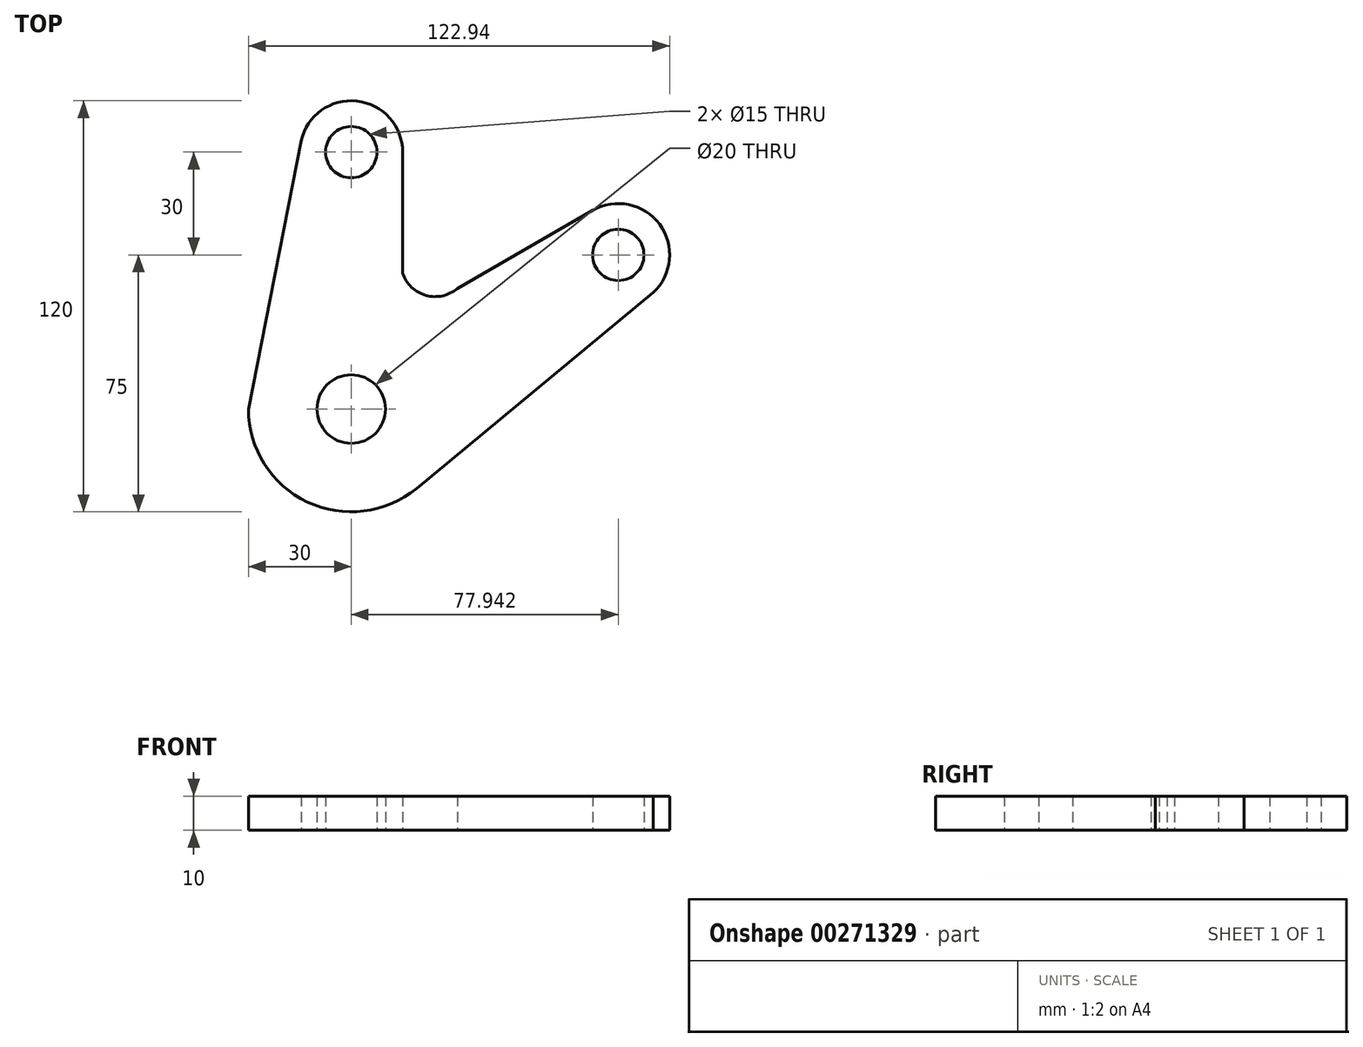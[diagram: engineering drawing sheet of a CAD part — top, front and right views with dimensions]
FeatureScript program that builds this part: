
annotation { "Feature Type Name" : "Feature", "Feature Type Description" : "" }
export const myFeature = defineFeature(function(context is Context, id is Id, definition is map)
    precondition{}
    {
        {
            var Q0;
            Q0=qCreatedBy(makeId("Top.planeOp"),FACE);
            var sketch = newSketch(context, id + "F0", { "sketchPlane" : qUnion([Q0])});
            skCircle(sketch, "E0", {"center": v(0, 0) * mm, "radius": 10 * mm});
            skLineSegment(sketch, "E1", {"start": v(0, 0) * mm, "end": v(77.94, 45) * mm, "construction": true});
            skLineSegment(sketch, "E2", {"start": v(0, 0) * mm, "end": v(0, 75) * mm, "construction": true});
            skCircle(sketch, "E3", {"center": v(0, 75) * mm, "radius": 7.5 * mm});
            skCircle(sketch, "E4", {"center": v(77.94, 45) * mm, "radius": 7.5 * mm});
            skArc(sketch, "E5", {"start": v(-30, 0) * mm, "mid": v(-12.82, -27.12) * mm, "end": v(19.05, -23.18) * mm});
            skArc(sketch, "E6", {"start": v(15, 75) * mm, "mid": v(1.66, 89.9) * mm, "end": v(-14.63, 78.3) * mm});
            skArc(sketch, "E7", {"start": v(88.16, 34.02) * mm, "mid": v(90, 53.92) * mm, "end": v(70.44, 58) * mm});
            skLineSegment(sketch, "E8", {"start": v(-14.63, 78.3) * mm, "end": v(-30, 0) * mm});
            skLineSegment(sketch, "E9", {"start": v(88.16, 34.02) * mm, "end": v(19.05, -23.18) * mm});
            skLineSegment(sketch, "E10", {"start": v(15, 75) * mm, "end": v(15, 39.65) * mm});
            skLineSegment(sketch, "E11", {"start": v(70.44, 58) * mm, "end": v(30.65, 35.02) * mm});
            skArc(sketch, "E12", {"start": v(15, 39.65) * mm, "mid": v(21.8, 33.19) * mm, "end": v(30.95, 35.19) * mm});
            skSolve(sketch);
        }
        {
            var Q0;
            Q0 = qSketchRegion(id + "F0", true);
            extrude(context, id + "F1", {"entities" : qUnion([Q0]), "depth" : 10 * mm});
        }
    });
